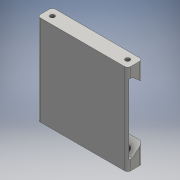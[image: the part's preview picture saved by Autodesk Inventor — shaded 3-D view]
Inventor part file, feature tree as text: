
AUTODESK INVENTOR PART (.ipt)
format: ipt  version: 2016 (Build 200138000, 138)  size: 171,520 bytes
history: native  units: mm
features: extrude x3, fillet x2, sketch x2
ambient origin geometry x8: Origin, YZ Plane, XZ Plane, XY Plane, X Axis, Y Axis, Z Axis, Center Point
bodies: Solid1 (feature_tree)
feature tree (7):
  extrude  "Block"  Depth=60.0mm
  extrude  "Tripod Slot"  Depth=2.0mm
  extrude  "Plastic Thinning"  Depth=2.0mm
  fillet  "Strength"  Radius=5.0mm
  fillet  "Fillet3"  Radius=5.0mm
  sketch  "Sketch2"  dims[d0=60.0mm d1=60.0mm]
  sketch  "Sketch3"  dims[d2=5.0mm d3=5.0mm d4=5.0mm d5=5.0mm d6=5.0mm d7=5.0mm d8=5.0mm d9=5.0mm d10=3.0mm d11=3.0mm d12=3.0mm d13=3.0mm d14=60.0mm d15=0.0mm d17=17.25mm d18=17.25mm d19=8.9mm d20=23.25mm d21=23.25mm d22=2.0mm d23=2.0mm d24=60.0mm d25=0.0mm d26=5.0mm d27=90.0deg d28=5.0mm d29=90.0deg d30=7.5mm d31=90.0deg d32=7.5mm d33=90.0deg d34=25.0mm d35=25.0mm d36=25.0mm d37=25.0mm d38=90.0deg d39=90.0deg d40=4.861193mm d41=4.861193mm d42=55.0mm d43=60.0mm d44=0.0mm d45=3.0mm d46=10.0mm d47=2.0mm]
